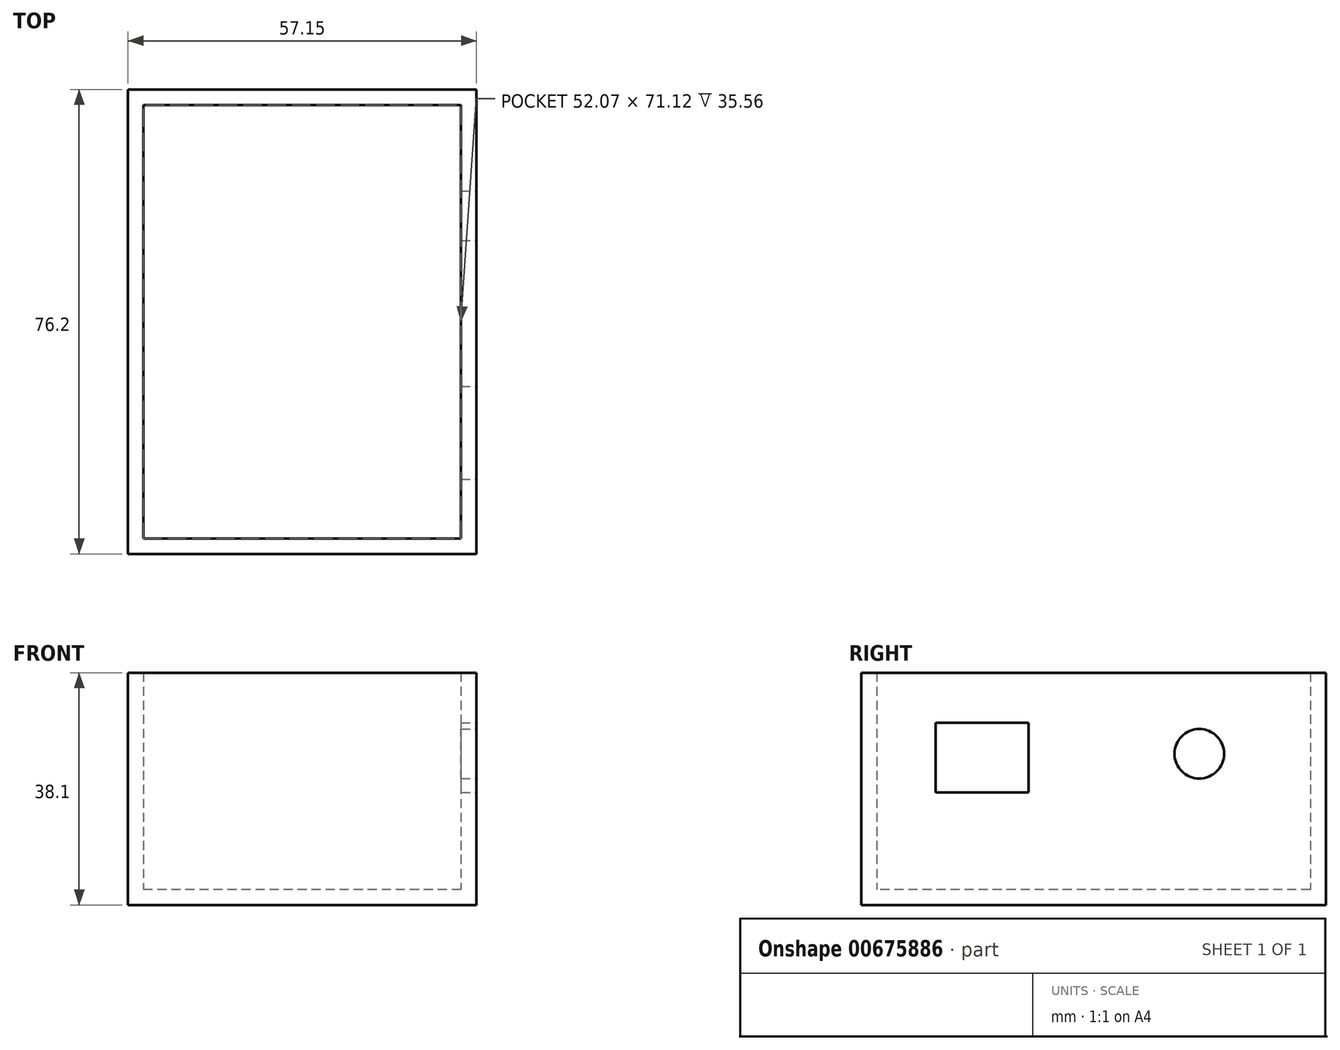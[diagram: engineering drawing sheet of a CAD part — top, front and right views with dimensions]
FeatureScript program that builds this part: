
annotation { "Feature Type Name" : "Feature", "Feature Type Description" : "" }
export const myFeature = defineFeature(function(context is Context, id is Id, definition is map)
    precondition{}
    {
        {
            var Q0;
            Q0=qCreatedBy(makeId("Top.planeOp"),FACE);
            var sketch = newSketch(context, id + "F0", { "sketchPlane" : qUnion([Q0])});
            skLineSegment(sketch, "E0.bottom", {"start": v(28.57, 38.1) * mm, "end": v(-28.58, 38.1) * mm});
            skLineSegment(sketch, "E0.top", {"start": v(28.58, -38.1) * mm, "end": v(-28.57, -38.1) * mm});
            skLineSegment(sketch, "E0.left", {"start": v(28.57, 38.1) * mm, "end": v(28.58, -38.1) * mm});
            skLineSegment(sketch, "E0.right", {"start": v(-28.58, 38.1) * mm, "end": v(-28.57, -38.1) * mm});
            skPoint(sketch, "E0.middle", {"position": v(0, 0) * mm});
            skSolve(sketch);
        }
        {
            var Q0;
            Q0 = qSketchRegion(id + "F0", true);
            extrude(context, id + "F1", {"entities" : qUnion([Q0]), "depth" : 38.1 * mm, "offsetDistance" : 25.4 * mm});
        }
        {
            var Q0;
            Q0=makeQuery(id+"F1.opExtrude","CAP_FACE",FACE,{"disambiguationData":[OSD([sQuery(id+"F0.wireOp",EDGE,"E0.bottom"),sQuery(id+"F0.wireOp",EDGE,"E0.top"),sQuery(id+"F0.wireOp",EDGE,"E0.left"),sQuery(id+"F0.wireOp",EDGE,"E0.right")])],"isStart":false});
            shell(context, id + "F2", {"entities" : qUnion([Q0]), "thickness" : 2.54 * mm});
        }
        {
            var Q0;
            Q0=makeQuery(id+"F1.opExtrude","SWEPT_FACE",FACE,{"disambiguationData":[OSD([sQuery(id+"F0.wireOp",EDGE,"E0.left")])]});
            var sketch = newSketch(context, id + "F3", { "sketchPlane" : qUnion([Q0])});
            skLineSegment(sketch, "E1.bottom", {"start": v(-25.88, 29.9) * mm, "end": v(-10.64, 29.9) * mm});
            skLineSegment(sketch, "E1.top", {"start": v(-25.88, 18.47) * mm, "end": v(-10.64, 18.47) * mm});
            skLineSegment(sketch, "E1.left", {"start": v(-25.88, 29.9) * mm, "end": v(-25.88, 18.47) * mm});
            skLineSegment(sketch, "E1.right", {"start": v(-10.64, 29.9) * mm, "end": v(-10.64, 18.47) * mm});
            skSolve(sketch);
        }
        {
            var Q0;
            Q0=makeQuery(id+"F3.imprint","IMPRINT",FACE,{"disambiguationData":[TD([[makeQuery(id+"F3.imprint","IMPRINT",EDGE,{"derivedFrom":sQuery(id+"F3.wireOp",EDGE,"E1.bottom")}),-1.0]])]});
            extrude(context, id + "F4", {"entities" : qUnion([Q0]), "operationType" : NewBodyOperationType.REMOVE, "oppositeDirection" : true, "depth" : 25.4 * mm, "offsetDistance" : 25.4 * mm});
        }
        {
            var Q0;
            Q0=makeQuery(id+"F1.opExtrude","SWEPT_FACE",FACE,{"disambiguationData":[OSD([sQuery(id+"F0.wireOp",EDGE,"E0.left")])]});
            var sketch = newSketch(context, id + "F5", { "sketchPlane" : qUnion([Q0])});
            skPoint(sketch, "E2", {"position": v(17.35, 24.8) * mm});
            skSolve(sketch);
        }
        {
            var Q0;
            Q0=sQuery(id+"F5.wireOp",VERTEX,"E2");
            var Q1;
            Q1=makeQuery(id+"F1.opExtrude","SWEPT_BODY",BODY,{"disambiguationData":[OSD([sQuery(id+"F0.wireOp",EDGE,"E0.bottom"),sQuery(id+"F0.wireOp",EDGE,"E0.top"),sQuery(id+"F0.wireOp",EDGE,"E0.left"),sQuery(id+"F0.wireOp",EDGE,"E0.right")])]});
            hole(context, id + "F6", {"style" : HoleStyle.SIMPLE, "endStyle" : HoleEndStyle.BLIND, "holeDiameter" : 8.13 * mm, "majorDiameter" : 6.35 * mm, "holeDepth" : 12.7 * mm, "isTappedThrough" : true, "tappedDepth" : 12.7 * mm, "tapClearance" : 3, "locations" : qUnion([Q0]), "scope" : qUnion([Q1])});
        }
    });
